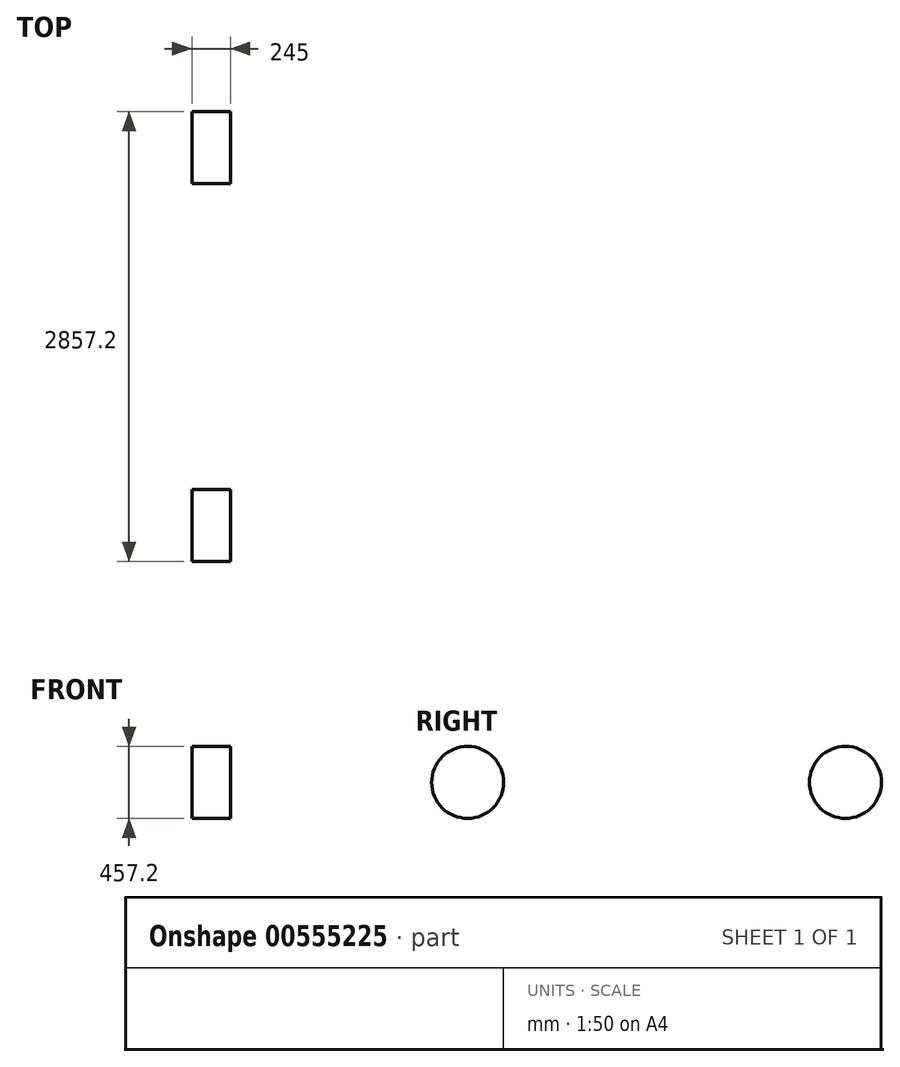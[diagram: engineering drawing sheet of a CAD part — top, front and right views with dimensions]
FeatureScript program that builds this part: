
annotation { "Feature Type Name" : "Feature", "Feature Type Description" : "" }
export const myFeature = defineFeature(function(context is Context, id is Id, definition is map)
    precondition{}
    {
        {
            var Q0;
            Q0=qCreatedBy(makeId("Top.planeOp"),FACE);
            cPlane(context, id + "F0", {"entities" : qUnion([Q0]), "cplaneType" : CPlaneType.OFFSET, "offset" : 228.6 * mm, "width" : 150 * mm, "height" : 150 * mm});
        }
        {
            var Q0;
            Q0=qCreatedBy(makeId("Top.planeOp"),FACE);
            cPlane(context, id + "F1", {"entities" : qUnion([Q0]), "cplaneType" : CPlaneType.OFFSET, "offset" : 50 * mm, "width" : 150 * mm, "height" : 150 * mm});
        }
        {
            var Q0;
            Q0=qCreatedBy(id+"F0.planeOp",FACE);
            var sketch = newSketch(context, id + "F2", { "sketchPlane" : qUnion([Q0])});
            skLineSegment(sketch, "E0", {"start": v(0, 0) * mm, "end": v(0, -2400) * mm, "construction": true});
            skLineSegment(sketch, "E1", {"start": v(0, 0) * mm, "end": v(900, 0) * mm, "construction": true});
            skLineSegment(sketch, "E2", {"start": v(0, -2400) * mm, "end": v(900, -2400) * mm, "construction": true});
            skLineSegment(sketch, "E3.bottom", {"start": v(900, -2171.4) * mm, "end": v(655, -2171.4) * mm});
            skLineSegment(sketch, "E3.top", {"start": v(900, -2628.6) * mm, "end": v(655, -2628.6) * mm});
            skLineSegment(sketch, "E3.left", {"start": v(900, -2171.4) * mm, "end": v(900, -2628.6) * mm});
            skLineSegment(sketch, "E3.right", {"start": v(655, -2171.4) * mm, "end": v(655, -2628.6) * mm});
            skPoint(sketch, "E3.middle", {"position": v(777.5, -2400) * mm});
            skLineSegment(sketch, "E4.bottom", {"start": v(900, 228.6) * mm, "end": v(655, 228.6) * mm});
            skLineSegment(sketch, "E4.top", {"start": v(900, -228.6) * mm, "end": v(655, -228.6) * mm});
            skLineSegment(sketch, "E4.left", {"start": v(900, 228.6) * mm, "end": v(900, -228.6) * mm});
            skLineSegment(sketch, "E4.right", {"start": v(655, 228.6) * mm, "end": v(655, -228.6) * mm});
            skPoint(sketch, "E4.middle", {"position": v(777.5, 0) * mm});
            skSolve(sketch);
        }
        {
            var Q0;
            Q0=sQuery(id+"F2.wireOp",VERTEX,"E1.end");
            var Q1;
            Q1=qCreatedBy(makeId("Right.planeOp"),FACE);
            cPlane(context, id + "F3", {"entities" : qUnion([Q0, Q1]), "cplaneType" : CPlaneType.PLANE_POINT, "offset" : 25 * mm, "width" : 150 * mm, "height" : 150 * mm});
        }
        {
            var Q0;
            Q0=qCreatedBy(makeId("Right.planeOp"),FACE);
            var Q1;
            Q1=sQuery(id+"F2.wireOp",VERTEX,"E2.end");
            cPlane(context, id + "F4", {"entities" : qUnion([Q0, Q1]), "cplaneType" : CPlaneType.PLANE_POINT, "offset" : 25 * mm, "width" : 150 * mm, "height" : 150 * mm});
        }
        {
            var Q0;
            Q0=qCreatedBy(id+"F3.planeOp",FACE);
            var sketch = newSketch(context, id + "F5", { "sketchPlane" : qUnion([Q0])});
            skCircle(sketch, "E5", {"center": v(0, 228.6) * mm, "radius": 228.6 * mm});
            skSolve(sketch);
        }
        {
            var Q0;
            Q0=qCreatedBy(id+"F4.planeOp",FACE);
            var sketch = newSketch(context, id + "F6", { "sketchPlane" : qUnion([Q0])});
            skCircle(sketch, "E6", {"center": v(-2400, 228.6) * mm, "radius": 228.6 * mm});
            skSolve(sketch);
        }
        {
            var Q0;
            Q0=makeQuery(id+"F6.imprint","IMPRINT",FACE,{"disambiguationData":[TD([[makeQuery(id+"F6.imprint","IMPRINT",EDGE,{"derivedFrom":sQuery(id+"F6.wireOp",EDGE,"E6")}),1.0]])]});
            var Q1;
            Q1=sQuery(id+"F2.wireOp",VERTEX,"E3.right.end");
            extrude(context, id + "F7", {"entities" : qUnion([Q0]), "endBound" : BoundingType.UP_TO_VERTEX, "oppositeDirection" : true, "depth" : 25 * mm, "endBoundEntityVertex" : qUnion([Q1]), "offsetDistance" : 25 * mm});
        }
        {
            var Q0;
            Q0=makeQuery(id+"F5.imprint","IMPRINT",FACE,{"disambiguationData":[TD([[makeQuery(id+"F5.imprint","IMPRINT",EDGE,{"derivedFrom":sQuery(id+"F5.wireOp",EDGE,"E5")}),1.0]])]});
            var Q1;
            Q1=sQuery(id+"F2.wireOp",VERTEX,"E4.top.end");
            extrude(context, id + "F8", {"entities" : qUnion([Q0]), "endBound" : BoundingType.UP_TO_VERTEX, "oppositeDirection" : true, "depth" : 25 * mm, "endBoundEntityVertex" : qUnion([Q1]), "offsetDistance" : 25 * mm});
        }
    });
